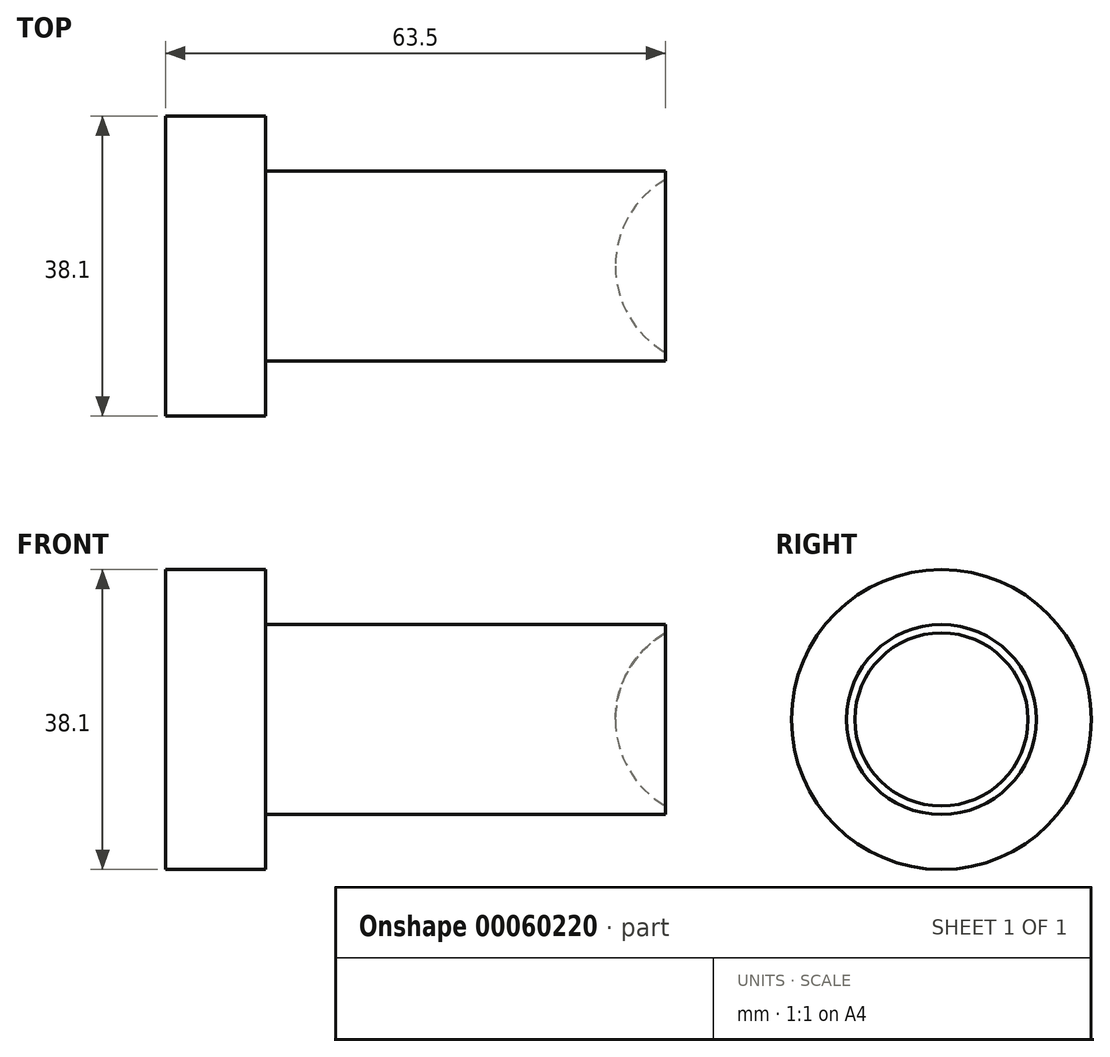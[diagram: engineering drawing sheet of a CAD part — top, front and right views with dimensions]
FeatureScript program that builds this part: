
annotation { "Feature Type Name" : "Feature", "Feature Type Description" : "" }
export const myFeature = defineFeature(function(context is Context, id is Id, definition is map)
    precondition{}
    {
        {
            var Q0;
            Q0=qCreatedBy(makeId("Front.planeOp"),FACE);
            var sketch = newSketch(context, id + "F0", { "sketchPlane" : qUnion([Q0])});
            skLineSegment(sketch, "E0", {"start": v(0, 0) * mm, "end": v(0, 19.05) * mm});
            skLineSegment(sketch, "E1", {"start": v(0, 19.05) * mm, "end": v(12.7, 19.05) * mm});
            skLineSegment(sketch, "E2", {"start": v(12.7, 19.05) * mm, "end": v(12.7, 12.06) * mm});
            skLineSegment(sketch, "E3", {"start": v(12.7, 12.07) * mm, "end": v(63.5, 12.07) * mm});
            skLineSegment(sketch, "E4", {"start": v(63.5, 12.07) * mm, "end": v(63.5, 11) * mm});
            skLineSegment(sketch, "E5", {"start": v(57.15, 0) * mm, "end": v(0, 0) * mm});
            skArc(sketch, "E6", {"start": v(63.5, 11) * mm, "mid": v(58.85, 6.35) * mm, "end": v(57.15, 0) * mm});
            skPoint(sketch, "E7.orphan", {"position": v(63.5, 0) * mm});
            skSolve(sketch);
        }
        {
            var Q0;
            Q0 = qSketchRegion(id + "F0", true);
            var Q1;
            Q1=sQuery(id+"F0.wireOp",EDGE,"E5");
            revolve(context, id + "F1", {"entities" : qUnion([Q0]), "axis" : qUnion([Q1]), "revolveType" : RevolveType.FULL});
        }
    });
